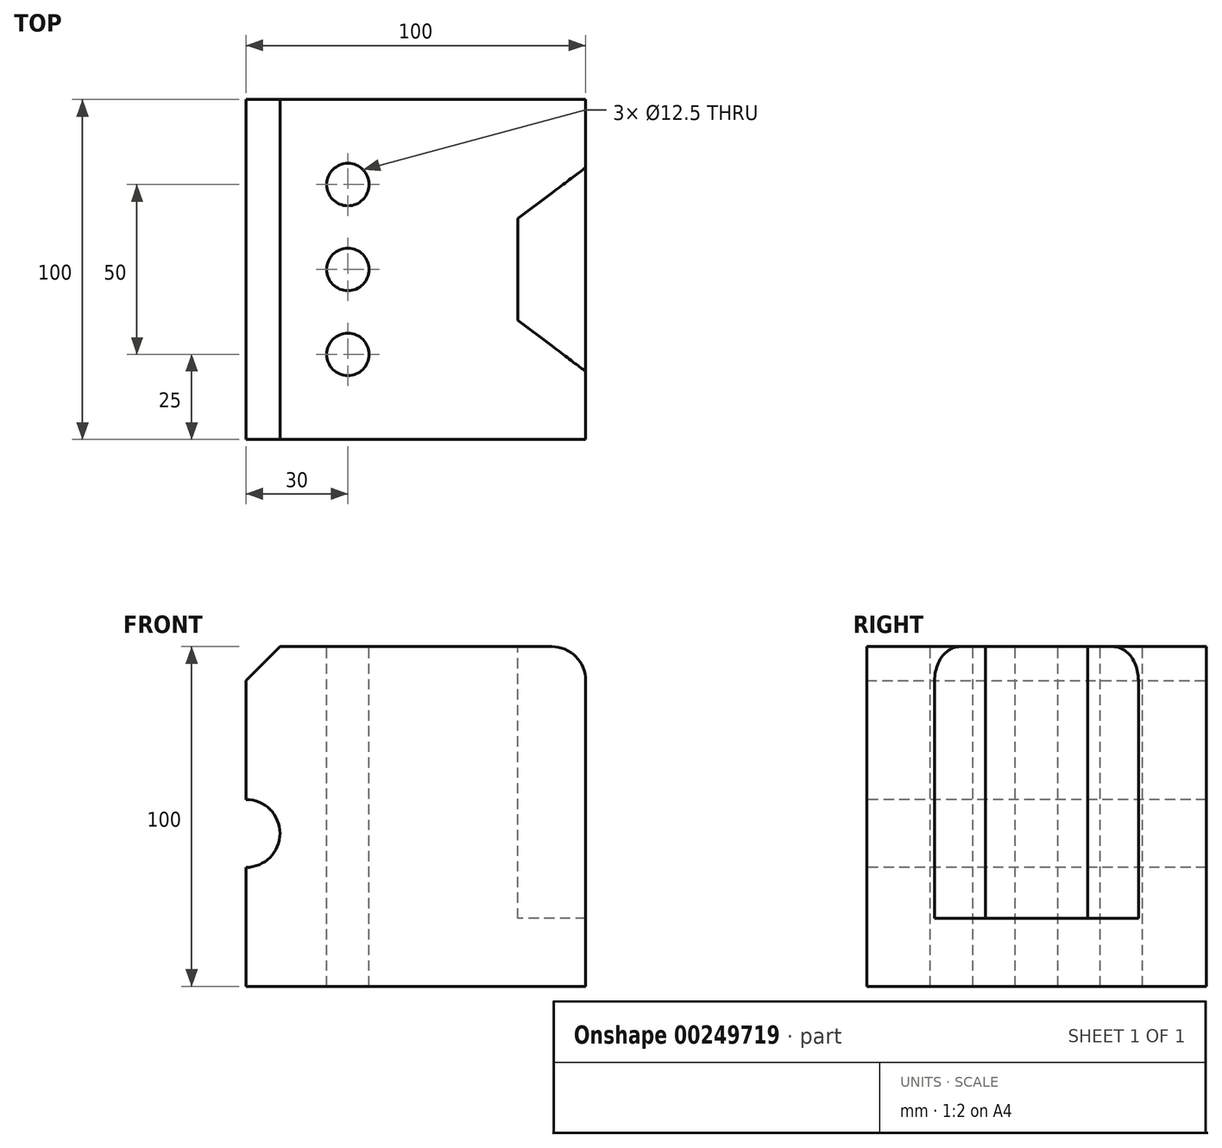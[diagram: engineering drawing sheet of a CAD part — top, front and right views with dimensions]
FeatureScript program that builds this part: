
annotation { "Feature Type Name" : "Feature", "Feature Type Description" : "" }
export const myFeature = defineFeature(function(context is Context, id is Id, definition is map)
    precondition{}
    {
        {
            var Q0;
            Q0=qCreatedBy(makeId("Top.planeOp"),FACE);
            var sketch = newSketch(context, id + "F0", { "sketchPlane" : qUnion([Q0])});
            skLineSegment(sketch, "E0.bottom", {"start": v(0, 0) * mm, "end": v(100, 0) * mm});
            skLineSegment(sketch, "E0.top", {"start": v(0, -100) * mm, "end": v(100, -100) * mm});
            skLineSegment(sketch, "E0.left", {"start": v(0, 0) * mm, "end": v(0, -100) * mm});
            skLineSegment(sketch, "E0.right", {"start": v(100, 0) * mm, "end": v(100, -100) * mm});
            skSolve(sketch);
        }
        {
            var Q0;
            Q0=makeQuery(id+"F0.imprint","IMPRINT",FACE,{"disambiguationData":[TD([[makeQuery(id+"F0.imprint","IMPRINT",EDGE,{"derivedFrom":sQuery(id+"F0.wireOp",EDGE,"E0.bottom")}),-1.0]])]});
            extrude(context, id + "F1", {"entities" : qUnion([Q0]), "depth" : 100 * mm});
        }
        {
            var Q0;
            Q0=makeQuery(id+"F1.opExtrude","SWEPT_FACE",FACE,{"disambiguationData":[OSD([sQuery(id+"F0.wireOp",EDGE,"E0.top")])]});
            var sketch = newSketch(context, id + "F2", { "sketchPlane" : qUnion([Q0])});
            skCircle(sketch, "E1", {"center": v(0, 45) * mm, "radius": 10 * mm});
            skSolve(sketch);
        }
        {
            var Q0;
            {var subQ0=sQuery(id+"F2.wireOp",EDGE,"E1");var subQ1=makeQuery(id+"F1.opExtrude","SWEPT_EDGE",EDGE,{"disambiguationData":[OSD([sQuery(id+"F0.wireOp",EDGE,"E0.top"),sQuery(id+"F0.wireOp",EDGE,"E0.left")])]});var subQ2=makeQuery(id+"F2.imprint","INTERSECT",VERTEX,{"disambiguationData":[OD(0.0)],"derivedFrom":[subQ1,subQ0]});Q0=makeQuery(id+"F2.imprint","IMPRINT",FACE,{"disambiguationData":[TD([[makeQuery(id+"F2.imprint","IMPRINT",EDGE,{"disambiguationData":[TD([[subQ2,-1.0]])],"derivedFrom":subQ0}),1.0]])]});}
            extrude(context, id + "F3", {"entities" : qUnion([Q0]), "operationType" : NewBodyOperationType.REMOVE, "endBound" : BoundingType.THROUGH_ALL, "oppositeDirection" : true, "depth" : 25 * mm});
        }
        {
            var Q0;
            Q0=makeQuery(id+"F1.opExtrude","CAP_FACE",FACE,{"disambiguationData":[OSD([sQuery(id+"F0.wireOp",EDGE,"E0.bottom"),sQuery(id+"F0.wireOp",EDGE,"E0.top"),sQuery(id+"F0.wireOp",EDGE,"E0.left"),sQuery(id+"F0.wireOp",EDGE,"E0.right")])],"isStart":false});
            var sketch = newSketch(context, id + "F4", { "sketchPlane" : qUnion([Q0])});
            skLineSegment(sketch, "E2", {"start": v(100, -20) * mm, "end": v(80, -35) * mm});
            skLineSegment(sketch, "E3", {"start": v(80, -35) * mm, "end": v(80, -65) * mm});
            skLineSegment(sketch, "E4", {"start": v(80, -65) * mm, "end": v(100, -80) * mm});
            skLineSegment(sketch, "E5", {"start": v(100, -80) * mm, "end": v(100, -20) * mm});
            skLineSegment(sketch, "E6", {"start": v(100, -50) * mm, "end": v(39.37, -50) * mm, "construction": true});
            skSolve(sketch);
        }
        {
            var Q0;
            Q0 = qSketchRegion(id + "F4", true);
            extrude(context, id + "F5", {"entities" : qUnion([Q0]), "operationType" : NewBodyOperationType.REMOVE, "oppositeDirection" : true, "depth" : 80 * mm});
        }
        {
            var Q0;
            {var subQ0=sQuery(id+"F0.wireOp",EDGE,"E0.right");var subQ1=sQuery(id+"F0.wireOp",EDGE,"E0.top");Q0=makeQuery(id+"F5.boolean.opBoolean","SPLIT",EDGE,{"disambiguationData":[TD([makeQuery(id+"F1.opExtrude","SWEPT_FACE",FACE,{"disambiguationData":[OSD([subQ1])]})])],"derivedFrom":makeQuery(id+"F1.opExtrude","CAP_EDGE",EDGE,{"disambiguationData":[OSD([subQ0])],"isStart":false})});}
            var Q1;
            {var subQ0=sQuery(id+"F0.wireOp",EDGE,"E0.bottom");var subQ1=sQuery(id+"F0.wireOp",EDGE,"E0.right");Q1=makeQuery(id+"F5.boolean.opBoolean","SPLIT",EDGE,{"disambiguationData":[TD([makeQuery(id+"F1.opExtrude","SWEPT_FACE",FACE,{"disambiguationData":[OSD([subQ0])]})])],"derivedFrom":makeQuery(id+"F1.opExtrude","CAP_EDGE",EDGE,{"disambiguationData":[OSD([subQ1])],"isStart":false})});}
            fillet(context, id + "F6", {"entities" : qUnion([Q0, Q1]), "radius" : 10 * mm, "tangentPropagation" : true, "allowEdgeOverflow" : false});
        }
        {
            var Q0;
            Q0=makeQuery(id+"F1.opExtrude","CAP_FACE",FACE,{"disambiguationData":[OSD([sQuery(id+"F0.wireOp",EDGE,"E0.bottom"),sQuery(id+"F0.wireOp",EDGE,"E0.top"),sQuery(id+"F0.wireOp",EDGE,"E0.left"),sQuery(id+"F0.wireOp",EDGE,"E0.right")])],"isStart":false});
            var sketch = newSketch(context, id + "F7", { "sketchPlane" : qUnion([Q0])});
            skCircle(sketch, "E7", {"center": v(30, -25) * mm, "radius": 6.25 * mm});
            skCircle(sketch, "E8.0.1.0", {"center": v(30, -50) * mm, "radius": 6.25 * mm});
            skCircle(sketch, "E8.0.2.0", {"center": v(30, -75) * mm, "radius": 6.25 * mm});
            skLineSegment(sketch, "E8.direction2", {"start": v(30, -25) * mm, "end": v(30, -50) * mm, "construction": true});
            skSolve(sketch);
        }
        {
            var Q0;
            Q0 = qSketchRegion(id + "F7", true);
            extrude(context, id + "F8", {"entities" : qUnion([Q0]), "operationType" : NewBodyOperationType.REMOVE, "endBound" : BoundingType.THROUGH_ALL, "oppositeDirection" : true, "depth" : 25 * mm});
        }
        {
            var Q0;
            Q0=makeQuery(id+"F1.opExtrude","CAP_EDGE",EDGE,{"disambiguationData":[OSD([sQuery(id+"F0.wireOp",EDGE,"E0.left")])],"isStart":false});
            chamfer(context, id + "F9", {"entities" : qUnion([Q0]), "chamferType" : ChamferType.OFFSET_ANGLE, "width" : 10 * mm, "oppositeDirection" : false, "angle" : 45 * degree, "tangentPropagation" : true});
        }
    });
